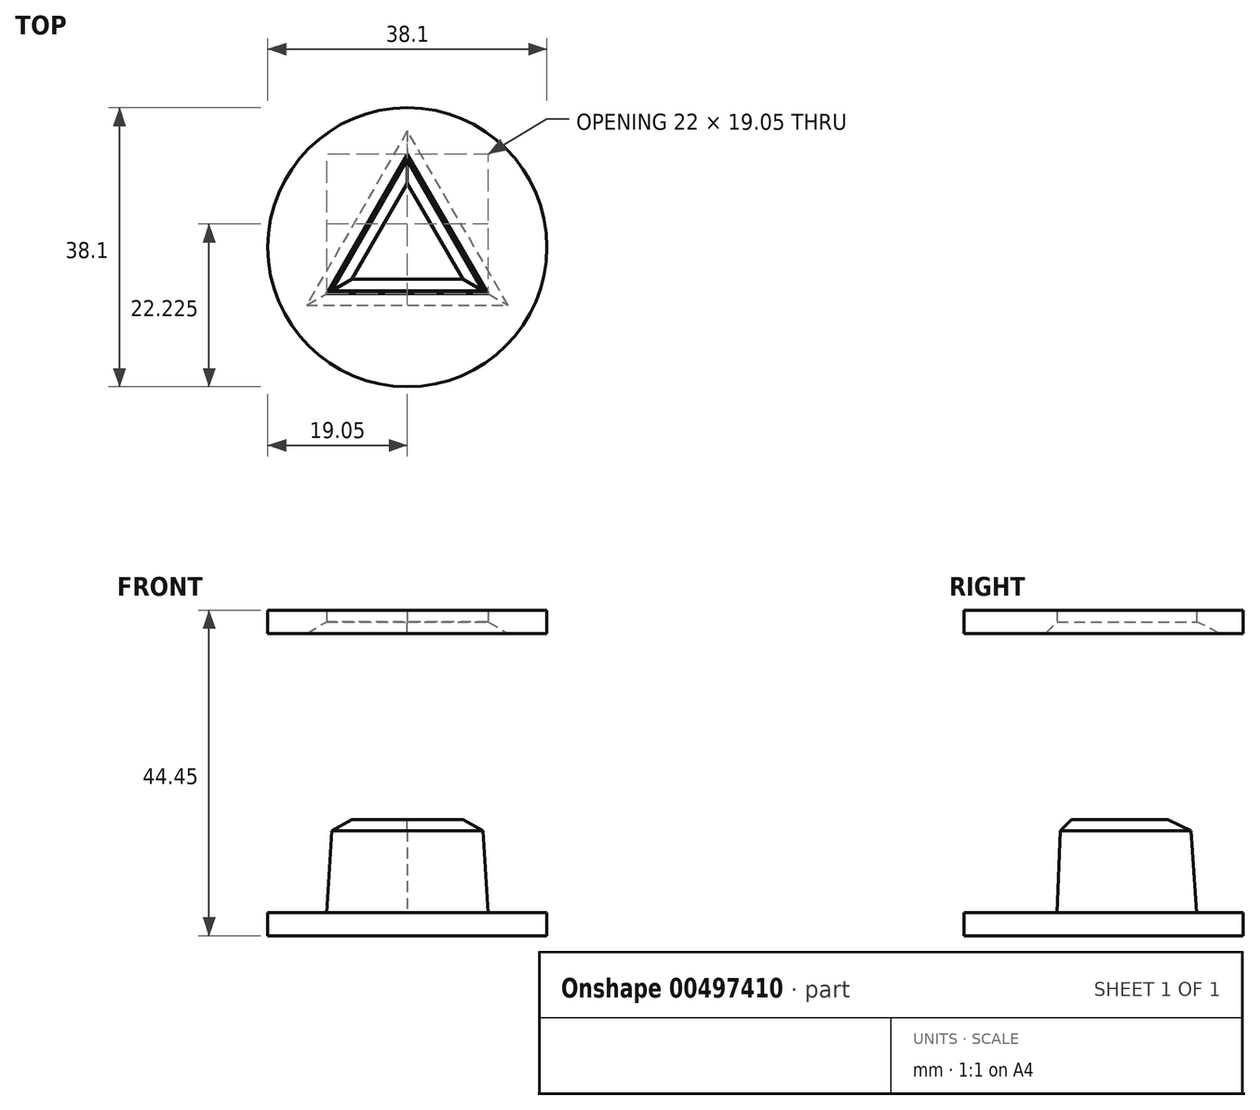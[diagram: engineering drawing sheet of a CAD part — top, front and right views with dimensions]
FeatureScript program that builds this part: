
annotation { "Feature Type Name" : "Feature", "Feature Type Description" : "" }
export const myFeature = defineFeature(function(context is Context, id is Id, definition is map)
    precondition{}
    {
        {
            var Q0;
            Q0=qCreatedBy(makeId("Top.planeOp"),FACE);
            var sketch = newSketch(context, id + "F0", { "sketchPlane" : qUnion([Q0])});
            skCircle(sketch, "E0", {"center": v(0, 0) * mm, "radius": 19.05 * mm});
            skCircle(sketch, "E1.cCircle", {"center": v(0, 0) * mm, "radius": 12.7 * mm, "construction": true});
            skLineSegment(sketch, "E1.0", {"start": v(0, 12.7) * mm, "end": v(11, -6.35) * mm});
            skLineSegment(sketch, "E1.1", {"start": v(11, -6.35) * mm, "end": v(-11, -6.35) * mm});
            skLineSegment(sketch, "E1.2", {"start": v(-11, -6.35) * mm, "end": v(0, 12.7) * mm});
            skSolve(sketch);
        }
        {
            var Q0;
            Q0=makeQuery(id+"F0.imprint","IMPRINT",FACE,{"disambiguationData":[TD([[makeQuery(id+"F0.imprint","IMPRINT",EDGE,{"derivedFrom":sQuery(id+"F0.wireOp",EDGE,"E0")}),1.0]])]});
            var Q1;
            Q1=makeQuery(id+"F0.imprint","IMPRINT",FACE,{"disambiguationData":[TD([[makeQuery(id+"F0.imprint","IMPRINT",EDGE,{"derivedFrom":sQuery(id+"F0.wireOp",EDGE,"E1.0")}),-1.0]])]});
            extrude(context, id + "F1", {"entities" : qUnion([Q0, Q1]), "depth" : 3.17 * mm, "offsetDistance" : 25.4 * mm});
        }
        {
            var Q0;
            Q0=makeQuery(id+"F1.opExtrude","CAP_FACE",FACE,{"disambiguationData":[OSD([sQuery(id+"F0.wireOp",EDGE,"E0")])],"isStart":false});
            var sketch = newSketch(context, id + "F2", { "sketchPlane" : qUnion([Q0])});
            skLineSegment(sketch, "E2.0", {"start": v(0, 12.7) * mm, "end": v(11, -6.35) * mm});
            skLineSegment(sketch, "E3.0", {"start": v(-11, -6.35) * mm, "end": v(0, 12.7) * mm});
            skLineSegment(sketch, "E4.0", {"start": v(11, -6.35) * mm, "end": v(-11, -6.35) * mm});
            skSolve(sketch);
        }
        {
            var Q0;
            Q0=makeQuery(id+"F2.imprint","IMPRINT",FACE,{"disambiguationData":[TD([[makeQuery(id+"F2.imprint","IMPRINT",EDGE,{"derivedFrom":sQuery(id+"F2.wireOp",EDGE,"E2.0")}),-1.0]])]});
            extrude(context, id + "F3", {"entities" : qUnion([Q0]), "operationType" : NewBodyOperationType.ADD, "depth" : 12.7 * mm, "offsetDistance" : 25.4 * mm, "hasDraft" : true, "draftAngle" : 2 * degree, "draftPullDirection" : true});
        }
        {
            var Q0;
            Q0=makeQuery(id+"F3.opExtrude","CAP_FACE",FACE,{"disambiguationData":[OSD([sQuery(id+"F2.wireOp",EDGE,"E2.0"),sQuery(id+"F2.wireOp",EDGE,"E3.0"),sQuery(id+"F2.wireOp",EDGE,"E4.0")])],"isStart":false});
            cPlane(context, id + "F4", {"entities" : qUnion([Q0]), "cplaneType" : CPlaneType.OFFSET, "offset" : 25.4 * mm, "width" : 152.4 * mm, "height" : 152.4 * mm});
        }
        {
            var Q0;
            Q0=qCreatedBy(id+"F4.planeOp",FACE);
            var sketch = newSketch(context, id + "F5", { "sketchPlane" : qUnion([Q0])});
            skCircle(sketch, "E5.0", {"center": v(0, 0) * mm, "radius": 19.05 * mm});
            skLineSegment(sketch, "E6.0", {"start": v(0, 12.7) * mm, "end": v(11, -6.35) * mm});
            skLineSegment(sketch, "E7.0", {"start": v(-11, -6.35) * mm, "end": v(0, 12.7) * mm});
            skLineSegment(sketch, "E8.0", {"start": v(11, -6.35) * mm, "end": v(-11, -6.35) * mm});
            skSolve(sketch);
        }
        {
            var Q0;
            Q0=makeQuery(id+"F5.imprint","IMPRINT",FACE,{"disambiguationData":[TD([[makeQuery(id+"F5.imprint","IMPRINT",EDGE,{"derivedFrom":sQuery(id+"F5.wireOp",EDGE,"E5.0")}),1.0]])]});
            extrude(context, id + "F6", {"entities" : qUnion([Q0]), "depth" : 3.17 * mm, "offsetDistance" : 25.4 * mm});
        }
        {
            var Q0;
            Q0=makeQuery(id+"F3.opExtrude","CAP_EDGE",EDGE,{"disambiguationData":[OSD([sQuery(id+"F2.wireOp",EDGE,"E2.0")])],"isStart":false});
            var Q1;
            Q1=makeQuery(id+"F3.opExtrude","CAP_EDGE",EDGE,{"disambiguationData":[OSD([sQuery(id+"F2.wireOp",EDGE,"E4.0")])],"isStart":false});
            var Q2;
            Q2=makeQuery(id+"F3.opExtrude","CAP_EDGE",EDGE,{"disambiguationData":[OSD([sQuery(id+"F2.wireOp",EDGE,"E3.0")])],"isStart":false});
            var Q3;
            Q3=makeQuery(id+"F6.opExtrude","CAP_EDGE",EDGE,{"disambiguationData":[OSD([sQuery(id+"F5.wireOp",EDGE,"E7.0")])],"isStart":true});
            var Q4;
            Q4=makeQuery(id+"F6.opExtrude","CAP_EDGE",EDGE,{"disambiguationData":[OSD([sQuery(id+"F5.wireOp",EDGE,"E6.0")])],"isStart":true});
            var Q5;
            Q5=makeQuery(id+"F6.opExtrude","CAP_EDGE",EDGE,{"disambiguationData":[OSD([sQuery(id+"F5.wireOp",EDGE,"E8.0")])],"isStart":true});
            chamfer(context, id + "F7", {"entities" : qUnion([Q0, Q1, Q2, Q3, Q4, Q5]), "width" : 1.59 * mm, "tangentPropagation" : true});
        }
    });
